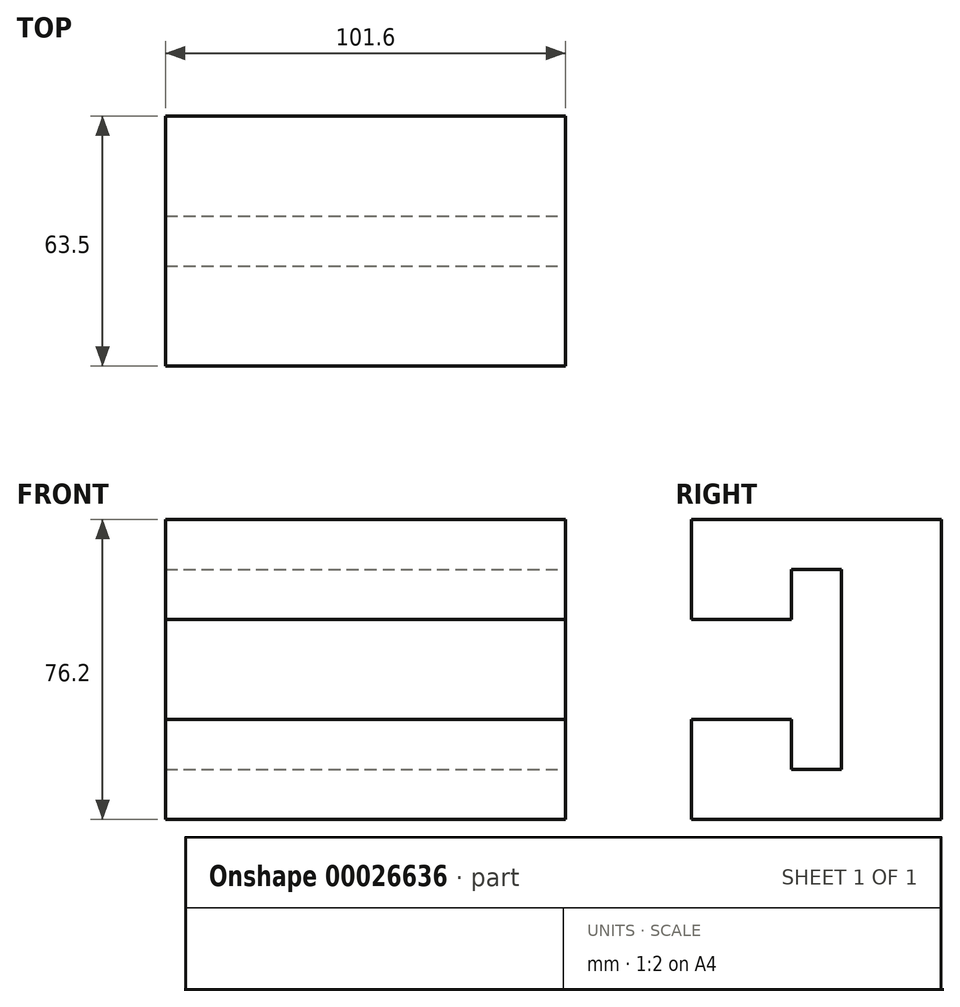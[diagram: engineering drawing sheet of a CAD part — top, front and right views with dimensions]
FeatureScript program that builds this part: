
annotation { "Feature Type Name" : "Feature", "Feature Type Description" : "" }
export const myFeature = defineFeature(function(context is Context, id is Id, definition is map)
    precondition{}
    {
        {
            var Q0;
            Q0=qCreatedBy(makeId("Front.planeOp"),FACE);
            var sketch = newSketch(context, id + "F0", { "sketchPlane" : qUnion([Q0])});
            skLineSegment(sketch, "E0.bottom", {"start": v(-51.7, 40.33) * mm, "end": v(49.9, 40.33) * mm});
            skLineSegment(sketch, "E0.top", {"start": v(-51.7, -35.87) * mm, "end": v(49.9, -35.87) * mm});
            skLineSegment(sketch, "E0.left", {"start": v(-51.7, 40.33) * mm, "end": v(-51.7, -35.87) * mm});
            skLineSegment(sketch, "E0.right", {"start": v(49.9, 40.33) * mm, "end": v(49.9, -35.87) * mm});
            skSolve(sketch);
        }
        {
            var Q0;
            Q0=makeQuery(id+"F0.imprint","IMPRINT",FACE,{"disambiguationData":[TD([[makeQuery(id+"F0.imprint","IMPRINT",EDGE,{"derivedFrom":sQuery(id+"F0.wireOp",EDGE,"E0.bottom")}),-1.0]])]});
            extrude(context, id + "F1", {"entities" : qUnion([Q0]), "depth" : 63.5 * mm});
        }
        {
            var Q0;
            Q0=makeQuery(id+"F1.opExtrude","SWEPT_FACE",FACE,{"disambiguationData":[OSD([sQuery(id+"F0.wireOp",EDGE,"E0.right")])]});
            var sketch = newSketch(context, id + "F2", { "sketchPlane" : qUnion([Q0])});
            skLineSegment(sketch, "E1", {"start": v(-25.4, -23.17) * mm, "end": v(-38.1, -23.17) * mm});
            skLineSegment(sketch, "E2.MirrorCS", {"start": v(-25.4, 27.63) * mm, "end": v(-38.1, 27.63) * mm});
            skLineSegment(sketch, "E3", {"start": v(-38.1, -23.17) * mm, "end": v(-38.1, -10.47) * mm});
            skLineSegment(sketch, "E4", {"start": v(-38.1, -10.47) * mm, "end": v(-63.5, -10.47) * mm});
            skLineSegment(sketch, "E5.MirrorCS", {"start": v(-38.1, 14.93) * mm, "end": v(-63.5, 14.93) * mm});
            skPoint(sketch, "E6.orphan", {"position": v(-63.5, 2.23) * mm});
            skLineSegment(sketch, "E7.trimOffspring", {"start": v(-38.1, 14.93) * mm, "end": v(-38.1, 27.63) * mm});
            skPoint(sketch, "E8.orphan", {"position": v(-25.4, -35.87) * mm});
            skPoint(sketch, "E9.orphan", {"position": v(0, 2.23) * mm});
            skPoint(sketch, "E10.start.orphan", {"position": v(-25.4, -10.47) * mm});
            skLineSegment(sketch, "E11", {"start": v(-25.4, -23.17) * mm, "end": v(-25.4, 27.63) * mm});
            skSolve(sketch);
        }
        {
            var Q0;
            Q0=makeQuery(id+"F2.imprint","IMPRINT",FACE,{"disambiguationData":[TD([[makeQuery(id+"F2.imprint","IMPRINT",EDGE,{"derivedFrom":sQuery(id+"F2.wireOp",EDGE,"E1")}),-1.0]])]});
            extrude(context, id + "F3", {"entities" : qUnion([Q0]), "operationType" : NewBodyOperationType.REMOVE, "endBound" : BoundingType.THROUGH_ALL, "oppositeDirection" : true, "depth" : 25.4 * mm});
        }
    });
